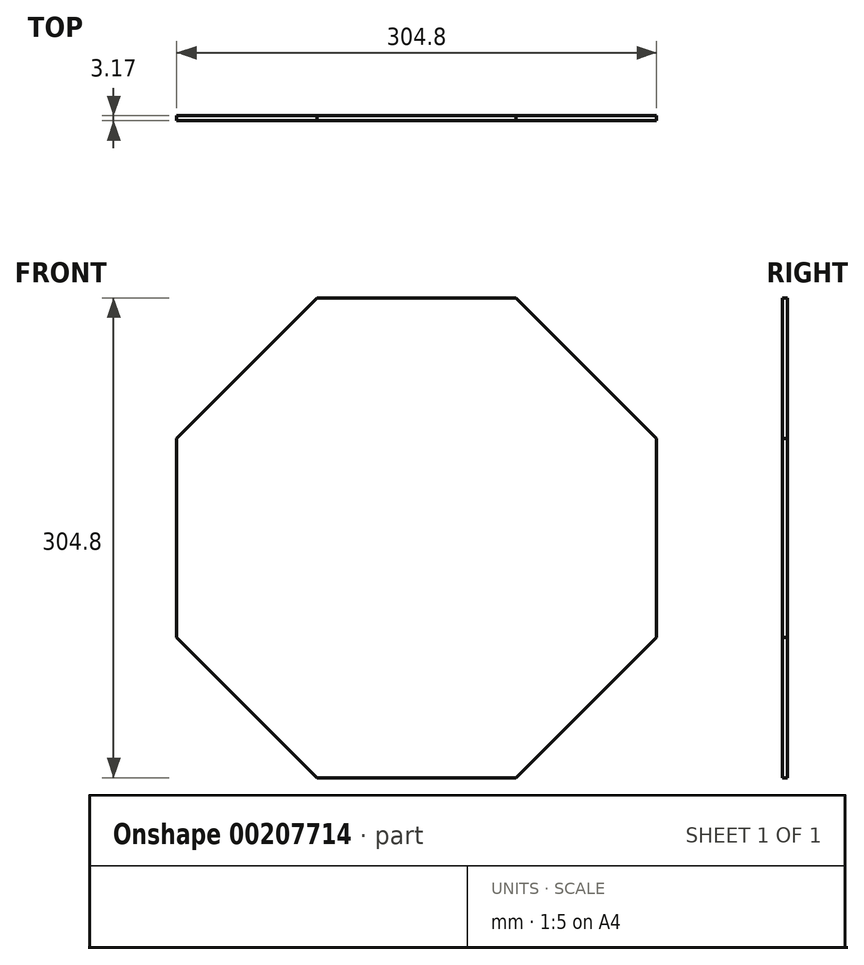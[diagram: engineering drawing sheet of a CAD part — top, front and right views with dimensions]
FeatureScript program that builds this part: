
annotation { "Feature Type Name" : "Feature", "Feature Type Description" : "" }
export const myFeature = defineFeature(function(context is Context, id is Id, definition is map)
    precondition{}
    {
        {
            var Q0;
            Q0=qCreatedBy(makeId("Front.planeOp"),FACE);
            var sketch = newSketch(context, id + "F0", { "sketchPlane" : qUnion([Q0])});
            skCircle(sketch, "E0.cCircle", {"center": v(0, 0) * mm, "radius": 152.4 * mm, "construction": true});
            skLineSegment(sketch, "E0.0", {"start": v(63.13, -152.4) * mm, "end": v(-63.13, -152.4) * mm});
            skLineSegment(sketch, "E0.1", {"start": v(-63.13, -152.4) * mm, "end": v(-152.4, -63.13) * mm});
            skLineSegment(sketch, "E0.2", {"start": v(-152.4, -63.13) * mm, "end": v(-152.4, 63.13) * mm});
            skLineSegment(sketch, "E0.3", {"start": v(-152.4, 63.13) * mm, "end": v(-63.13, 152.4) * mm});
            skLineSegment(sketch, "E0.4", {"start": v(-63.13, 152.4) * mm, "end": v(63.13, 152.4) * mm});
            skLineSegment(sketch, "E0.5", {"start": v(63.13, 152.4) * mm, "end": v(152.4, 63.13) * mm});
            skLineSegment(sketch, "E0.6", {"start": v(152.4, 63.13) * mm, "end": v(152.4, -63.13) * mm});
            skLineSegment(sketch, "E0.7", {"start": v(152.4, -63.13) * mm, "end": v(63.13, -152.4) * mm});
            skPoint(sketch, "E0.0.midPoint", {"position": v(0, -152.4) * mm});
            skSolve(sketch);
        }
        {
            var Q0;
            Q0=makeQuery(id+"F0.imprint","IMPRINT",FACE,{"disambiguationData":[TD([[makeQuery(id+"F0.imprint","IMPRINT",EDGE,{"derivedFrom":sQuery(id+"F0.wireOp",EDGE,"E0.0")}),-1.0]])]});
            extrude(context, id + "F1", {"entities" : qUnion([Q0]), "depth" : 3.17 * mm});
        }
    });
